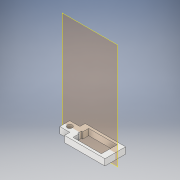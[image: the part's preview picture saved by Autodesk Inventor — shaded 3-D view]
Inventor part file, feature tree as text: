
AUTODESK INVENTOR PART (.ipt)
format: ipt  version: 2019 (Build 230136000, 136)  size: 174,080 bytes
history: native  units: in
note: dims shown in document units (in); Inventor stores cm internally (conversion verified against a paired STEP export)
features: sketch x4, plane x3, extrude x3
ambient origin geometry x8: Origin, YZ Plane, XZ Plane, XY Plane, X Axis, Y Axis, Z Axis, Center Point
bodies: Solid14 (feature_tree)
feature tree (10):
  plane  "Work Plane1"
  sketch  "Sketch1"  dims[d17=0.1969in d18=0.0in d19=0.4882in]
  plane  "Work Plane3"
  extrude  "Extrusion4"  Depth=0.4882in
  extrude  "Extrusion5"  Depth=0.1181in
  extrude  "Extrusion6"  Depth=0.315in
  plane  "Work Plane4"
  sketch  "Sketch6"  dims[d20=0.0394in d21=0.1181in]
  sketch  "Sketch7"  dims[d22=0.1969in d23=0.0in d24=0.315in]
  sketch  "Sketch8"  dims[d25=0.315in d26=0.1575in d27=0.1969in d28=0.0in]
